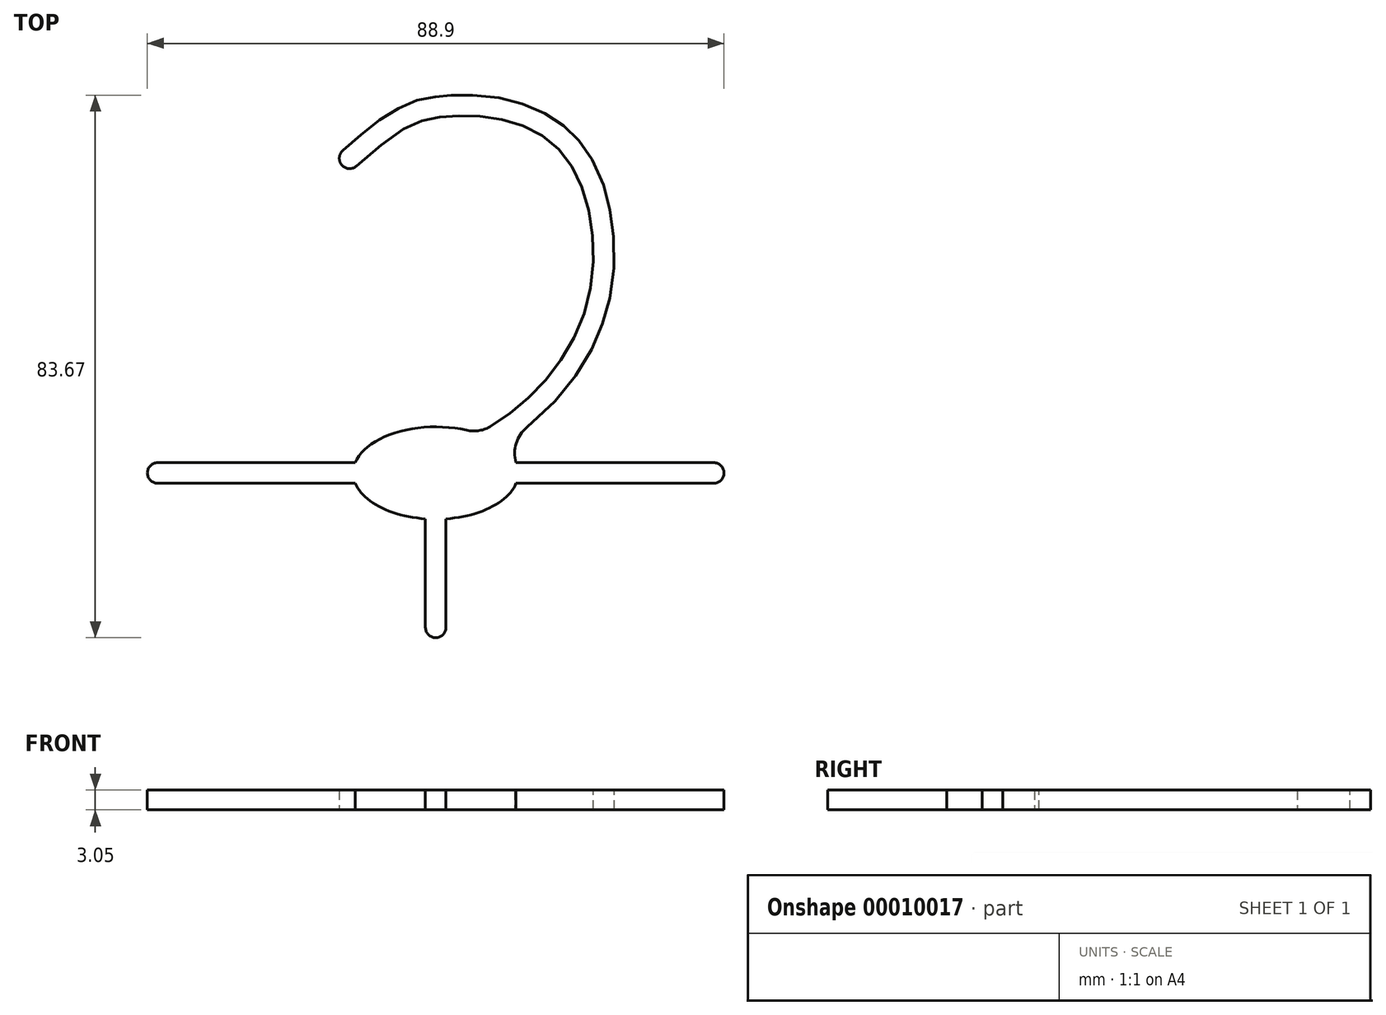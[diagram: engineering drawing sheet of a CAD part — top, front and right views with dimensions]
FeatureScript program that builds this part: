
annotation { "Feature Type Name" : "Feature", "Feature Type Description" : "" }
export const myFeature = defineFeature(function(context is Context, id is Id, definition is map)
    precondition{}
    {
        {
            var Q0;
            Q0=qCreatedBy(makeId("Top.planeOp"),FACE);
            var sketch = newSketch(context, id + "F0", { "sketchPlane" : qUnion([Q0])});
            skEllipticalArc(sketch, "E0", {});
            skLineSegment(sketch, "E1.bottom", {"start": v(-44.45, 1.59) * mm, "end": v(-12.38, 1.59) * mm});
            skLineSegment(sketch, "E1.top", {"start": v(-44.45, -1.59) * mm, "end": v(-12.38, -1.59) * mm});
            skLineSegment(sketch, "E1.left", {"start": v(-44.45, 1.59) * mm, "end": v(-44.45, -1.59) * mm});
            skLineSegment(sketch, "E1.right", {"start": v(44.45, 1.59) * mm, "end": v(44.45, -1.59) * mm});
            skLineSegment(sketch, "E2", {"start": v(0, 0) * mm, "end": v(0, -16.8) * mm, "construction": true});
            skLineSegment(sketch, "E3", {"start": v(0, 0) * mm, "end": v(-18.53, 0) * mm, "construction": true});
            skLineSegment(sketch, "E4.top", {"start": v(-1.59, -25.4) * mm, "end": v(1.59, -25.4) * mm});
            skLineSegment(sketch, "E4.left", {"start": v(-1.59, -7.06) * mm, "end": v(-1.59, -25.4) * mm});
            skFitSpline(sketch, "E5", {"points": [v(6.59, 6.09) * mm, v(15.75, 13.03) * mm, v(22.99, 24.93) * mm, v(23.8, 39.4) * mm, v(19.2, 49.69) * mm, v(10.61, 54.4) * mm, v(1.17, 54.95) * mm, v(-6.88, 51.76) * mm, v(-16.17, 44.12) * mm], "startDerivative": vector(75.94, 41.49) * mm, "endDerivative": vector(3.76, 16.11) * mm});
            skFitSpline(sketch, "E6.0", {"points": [v(8.1, 3.3) * mm, v(9.8, 4.22) * mm, v(13.16, 6.34) * mm, v(17.16, 9.8) * mm, v(20.1, 13.1) * mm, v(22.14, 15.85) * mm, v(23.93, 18.84) * mm, v(25.17, 21.53) * mm, v(25.97, 23.78) * mm, v(26.64, 26.1) * mm, v(27.2, 29.04) * mm, v(27.5, 32.6) * mm, v(27.44, 36.12) * mm, v(27.11, 38.98) * mm, v(26.7, 41.2) * mm, v(26.17, 43.37) * mm, v(25.29, 45.98) * mm, v(24.08, 48.4) * mm, v(22.9, 50.21) * mm, v(21.88, 51.48) * mm, v(20.75, 52.66) * mm, v(19.54, 53.7) * mm, v(18.25, 54.62) * mm, v(16.45, 55.69) * mm, v(14.55, 56.53) * mm, v(12.59, 57.17) * mm, v(10.6, 57.68) * mm, v(8.1, 58.1) * mm, v(5.66, 58.26) * mm, v(3.8, 58.27) * mm, v(2.44, 58.23) * mm, v(1.36, 58.16) * mm, v(0.53, 58.08) * mm, v(-0.3, 57.98) * mm, v(-1.37, 57.82) * mm, v(-2.69, 57.5) * mm, v(-4.04, 57.05) * mm, v(-5.42, 56.43) * mm, v(-6.83, 55.64) * mm, v(-8.3, 54.67) * mm, v(-9.86, 53.5) * mm, v(-11.46, 52.2) * mm, v(-13.04, 50.84) * mm, v(-14.54, 49.52) * mm, v(-15.66, 48.54) * mm, v(-16.43, 47.86) * mm, v(-16.93, 47.43) * mm, v(-17.28, 47.14) * mm, v(-17.46, 46.98) * mm, v(-17.55, 46.91) * mm, v(-17.6, 46.87) * mm, v(-17.65, 46.84) * mm, v(-17.67, 46.83) * mm, v(-17.68, 46.82) * mm, v(-17.69, 46.81) * mm, v(-17.69, 46.81) * mm, v(-17.69, 46.81) * mm, v(-17.69, 46.81) * mm, v(-17.7, 46.8) * mm, v(-17.7, 46.8) * mm, v(-17.71, 46.8) * mm, v(-17.73, 46.78) * mm, v(-17.75, 46.77) * mm, v(-17.79, 46.74) * mm, v(-17.83, 46.71) * mm, v(-17.9, 46.66) * mm, v(-17.96, 46.62) * mm, v(-18, 46.6) * mm]});
            skLineSegment(sketch, "E7", {"start": v(-15.61, 48.58) * mm, "end": v(-13.33, 46.36) * mm});
            skEllipticalArc(sketch, "E8.trimOffspring", {});
            skEllipticalArc(sketch, "E9.trimOffspring", {});
            skEllipticalArc(sketch, "E10.trimOffspring", {});
            skLineSegment(sketch, "E11.trimOffspring", {"start": v(1.59, -7.06) * mm, "end": v(1.59, -25.4) * mm});
            skLineSegment(sketch, "E12.trimOffspring", {"start": v(12.38, -1.59) * mm, "end": v(44.45, -1.59) * mm});
            skLineSegment(sketch, "E13.trimOffspring", {"start": v(12.38, 1.59) * mm, "end": v(44.45, 1.59) * mm});
            const initialGuessF0  = {"E0": [0, 0, -1, 0, 0.0127, 0.0071203422414569065, 4.167139182574682, 6.05834287176132], "E8.trimOffspring": [0, 0, -1, 0, 0.0127, 0.0071203422414569065, 3.3664350890080597, 3.8064204851313352], "E9.trimOffspring": [0, 0, -1, 0, 0.0127, 0.0071203422414569065, 0.2248424354182666, 1.4454684956268309], "E10.trimOffspring": [0, 0, -1, 0, 0.0127, 0.0071203422414569065, 1.6961241579629625, 2.9167502181715257]};
            skSetInitialGuess(sketch, initialGuessF0);
            skSolve(sketch);
        }
        {
            var Q0;
            Q0=makeQuery(id+"F0.imprint","IMPRINT",FACE,{"disambiguationData":[TD([[makeQuery(id+"F0.imprint","IMPRINT",EDGE,{"derivedFrom":sQuery(id+"F0.wireOp",EDGE,"E0")}),1.0]])]});
            extrude(context, id + "F1", {"entities" : qUnion([Q0]), "depth" : 3.05 * mm});
        }
        {
            var Q0;
            Q0=makeQuery(id+"F1.opExtrude","SWEPT_EDGE",EDGE,{"disambiguationData":[OSD([sQuery(id+"F0.wireOp",EDGE,"E6.0"),sQuery(id+"F0.wireOp",EDGE,"E7")])]});
            var Q1;
            Q1=makeQuery(id+"F1.opExtrude","SWEPT_EDGE",EDGE,{"disambiguationData":[OSD([sQuery(id+"F0.wireOp",EDGE,"E5"),sQuery(id+"F0.wireOp",EDGE,"E7")])]});
            fillet(context, id + "F2", {"entities" : qUnion([Q0, Q1]), "radius" : 1.59 * mm, "tangentPropagation" : true, "allowEdgeOverflow" : false});
        }
        {
            var Q0;
            Q0=makeQuery(id+"F1.opExtrude","SWEPT_EDGE",EDGE,{"disambiguationData":[OSD([sQuery(id+"F0.wireOp",EDGE,"E1.top"),sQuery(id+"F0.wireOp",EDGE,"E1.left")])]});
            var Q1;
            Q1=makeQuery(id+"F1.opExtrude","SWEPT_EDGE",EDGE,{"disambiguationData":[OSD([sQuery(id+"F0.wireOp",EDGE,"E1.bottom"),sQuery(id+"F0.wireOp",EDGE,"E1.left")])]});
            var Q2;
            Q2=makeQuery(id+"F1.opExtrude","SWEPT_EDGE",EDGE,{"disambiguationData":[OSD([sQuery(id+"F0.wireOp",EDGE,"E4.top"),sQuery(id+"F0.wireOp",EDGE,"E4.left")])]});
            var Q3;
            Q3=makeQuery(id+"F1.opExtrude","SWEPT_EDGE",EDGE,{"disambiguationData":[OSD([sQuery(id+"F0.wireOp",EDGE,"E4.top"),sQuery(id+"F0.wireOp",EDGE,"E11.trimOffspring")])]});
            var Q4;
            Q4=makeQuery(id+"F1.opExtrude","SWEPT_EDGE",EDGE,{"disambiguationData":[OSD([sQuery(id+"F0.wireOp",EDGE,"E1.right"),sQuery(id+"F0.wireOp",EDGE,"E12.trimOffspring")])]});
            var Q5;
            Q5=makeQuery(id+"F1.opExtrude","SWEPT_EDGE",EDGE,{"disambiguationData":[OSD([sQuery(id+"F0.wireOp",EDGE,"E1.right"),sQuery(id+"F0.wireOp",EDGE,"E13.trimOffspring")])]});
            fillet(context, id + "F3", {"entities" : qUnion([Q0, Q1, Q2, Q3, Q4, Q5]), "radius" : 1.59 * mm, "tangentPropagation" : true, "allowEdgeOverflow" : false});
        }
        {
            var Q0;
            Q0=makeQuery(id+"F1.opExtrude","SWEPT_EDGE",EDGE,{"disambiguationData":[OSD([sQuery(id+"F0.wireOp",EDGE,"E6.0"),sQuery(id+"F0.wireOp",EDGE,"E8.trimOffspring")])]});
            fillet(context, id + "F4", {"entities" : qUnion([Q0]), "radius" : 5.08 * mm, "tangentPropagation" : true, "allowEdgeOverflow" : false});
        }
        {
            var Q0;
            Q0=makeQuery(id+"F1.opExtrude","SWEPT_EDGE",EDGE,{"disambiguationData":[OSD([sQuery(id+"F0.wireOp",EDGE,"E0"),sQuery(id+"F0.wireOp",EDGE,"E5")])]});
            fillet(context, id + "F5", {"entities" : qUnion([Q0]), "radius" : 5.08 * mm, "tangentPropagation" : true, "allowEdgeOverflow" : false});
        }
    });
